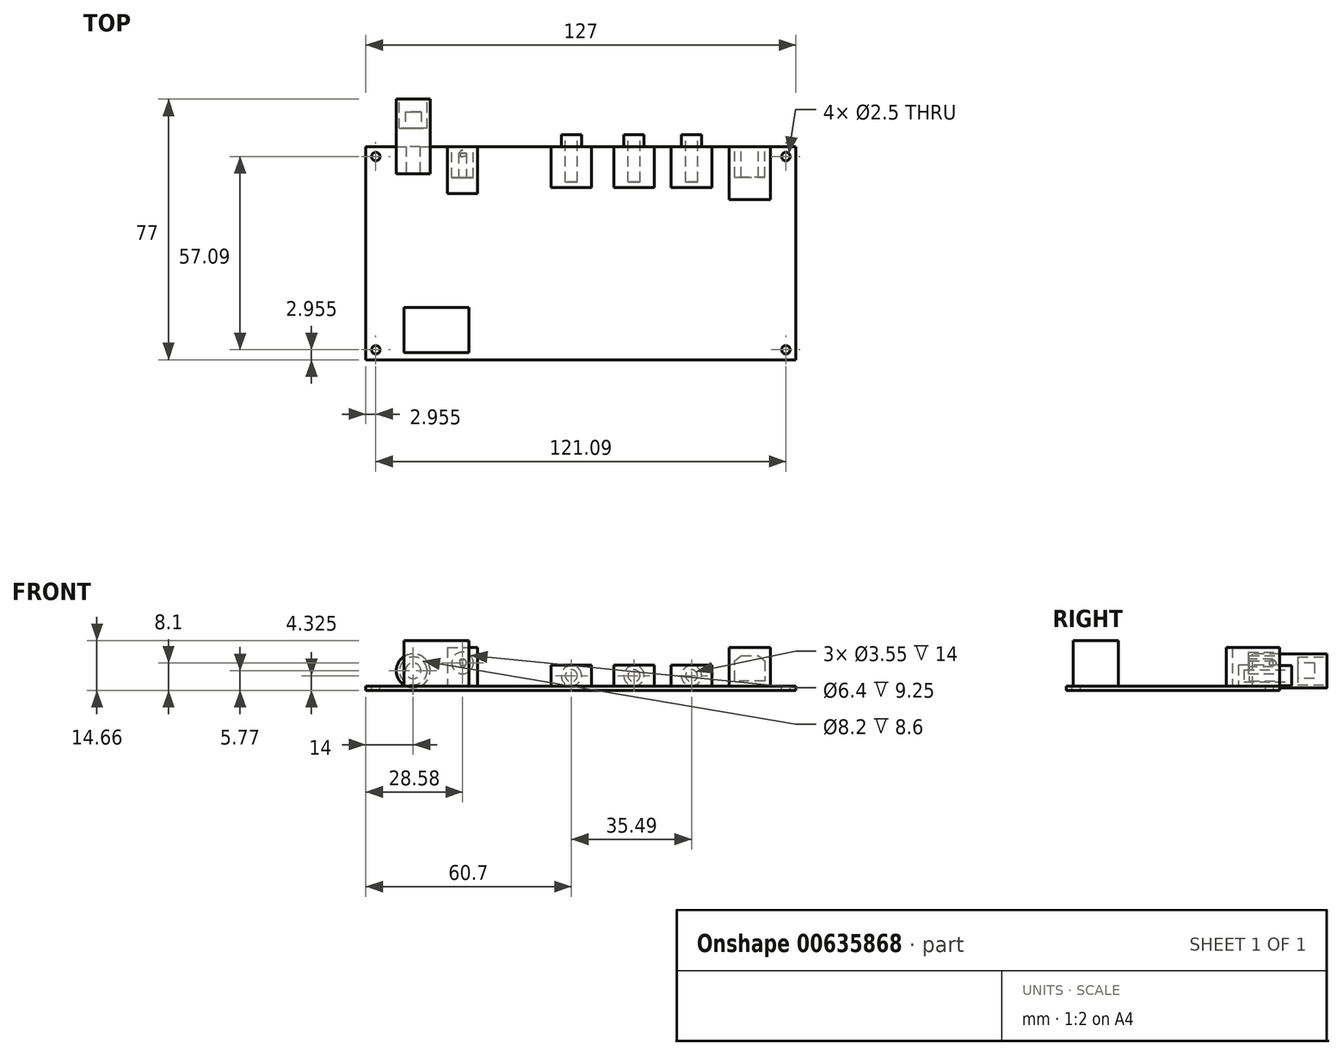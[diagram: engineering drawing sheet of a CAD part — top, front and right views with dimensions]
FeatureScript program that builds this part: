
annotation { "Feature Type Name" : "Feature", "Feature Type Description" : "" }
export const myFeature = defineFeature(function(context is Context, id is Id, definition is map)
    precondition{}
    {
        {
            var Q0;
            Q0=qCreatedBy(makeId("Top.planeOp"),FACE);
            var sketch = newSketch(context, id + "F0", { "sketchPlane" : qUnion([Q0])});
            skLineSegment(sketch, "E0.bottom", {"start": v(0, 0) * mm, "end": v(127, 0) * mm});
            skLineSegment(sketch, "E0.top", {"start": v(0, -63) * mm, "end": v(127, -63) * mm});
            skLineSegment(sketch, "E0.left", {"start": v(0, 0) * mm, "end": v(0, -63) * mm});
            skLineSegment(sketch, "E0.right", {"start": v(127, 0) * mm, "end": v(127, -63) * mm});
            skSolve(sketch);
        }
        {
            var Q0;
            Q0 = qSketchRegion(id + "F0", true);
            extrude(context, id + "F1", {"entities" : qUnion([Q0]), "depth" : 1.2 * mm, "offsetDistance" : 25 * mm});
        }
        {
            var Q0;
            Q0=makeQuery(id+"F1.opExtrude","CAP_FACE",FACE,{"disambiguationData":[OSD([sQuery(id+"F0.wireOp",EDGE,"E0.bottom"),sQuery(id+"F0.wireOp",EDGE,"E0.top"),sQuery(id+"F0.wireOp",EDGE,"E0.left"),sQuery(id+"F0.wireOp",EDGE,"E0.right")])],"isStart":false});
            var sketch = newSketch(context, id + "F2", { "sketchPlane" : qUnion([Q0]), "disableImprinting" : false});
            skLineSegment(sketch, "E1.bottom", {"start": v(2.95, -2.95) * mm, "end": v(124.05, -2.95) * mm, "construction": true});
            skLineSegment(sketch, "E1.top", {"start": v(2.95, -60.05) * mm, "end": v(124.05, -60.05) * mm, "construction": true});
            skLineSegment(sketch, "E1.left", {"start": v(2.95, -2.95) * mm, "end": v(2.95, -60.05) * mm, "construction": true});
            skLineSegment(sketch, "E1.right", {"start": v(124.05, -2.95) * mm, "end": v(124.05, -60.05) * mm, "construction": true});
            skCircle(sketch, "E2", {"center": v(2.95, -2.96) * mm, "radius": 2.96 * mm, "construction": true});
            skCircle(sketch, "E3", {"center": v(2.95, -60.05) * mm, "radius": 2.96 * mm, "construction": true});
            skCircle(sketch, "E4", {"center": v(124.05, -60.05) * mm, "radius": 2.96 * mm, "construction": true});
            skCircle(sketch, "E5", {"center": v(124.05, -2.96) * mm, "radius": 2.96 * mm, "construction": true});
            skPoint(sketch, "E6", {"position": v(63.5, 0) * mm});
            skPoint(sketch, "E7", {"position": v(0, -31.5) * mm});
            skPoint(sketch, "E8", {"position": v(63.5, -2.95) * mm});
            skPoint(sketch, "E9", {"position": v(2.95, -31.5) * mm});
            skCircle(sketch, "E10", {"center": v(2.95, -2.95) * mm, "radius": 1.25 * mm});
            skCircle(sketch, "E11", {"center": v(2.95, -60.05) * mm, "radius": 1.25 * mm});
            skCircle(sketch, "E12", {"center": v(124.05, -60.05) * mm, "radius": 1.25 * mm});
            skCircle(sketch, "E13", {"center": v(124.05, -2.95) * mm, "radius": 1.25 * mm});
            skSolve(sketch);
        }
        {
            var Q0;
            Q0 = qSketchRegion(id + "F2", true);
            extrude(context, id + "F3", {"entities" : qUnion([Q0]), "operationType" : NewBodyOperationType.REMOVE, "endBound" : BoundingType.UP_TO_NEXT, "oppositeDirection" : true, "depth" : 25 * mm, "offsetDistance" : 25 * mm});
        }
        {
            var Q0;
            Q0=makeQuery(id+"F1.opExtrude","CAP_FACE",FACE,{"disambiguationData":[OSD([sQuery(id+"F0.wireOp",EDGE,"E0.bottom"),sQuery(id+"F0.wireOp",EDGE,"E0.top"),sQuery(id+"F0.wireOp",EDGE,"E0.left"),sQuery(id+"F0.wireOp",EDGE,"E0.right")])],"isStart":false});
            var sketch = newSketch(context, id + "F4", { "sketchPlane" : qUnion([Q0])});
            skLineSegment(sketch, "E14.bottom", {"start": v(102.19, 0) * mm, "end": v(90.19, 0) * mm});
            skLineSegment(sketch, "E14.top", {"start": v(102.19, -12.13) * mm, "end": v(90.19, -12.13) * mm});
            skLineSegment(sketch, "E14.left", {"start": v(102.19, 0) * mm, "end": v(102.19, -12.13) * mm});
            skLineSegment(sketch, "E14.right", {"start": v(90.19, 0) * mm, "end": v(90.19, -12.13) * mm});
            skLineSegment(sketch, "E15.bottom", {"start": v(85.2, 0) * mm, "end": v(73.2, 0) * mm});
            skLineSegment(sketch, "E15.top", {"start": v(85.2, -12.13) * mm, "end": v(73.2, -12.13) * mm});
            skLineSegment(sketch, "E15.left", {"start": v(85.2, 0) * mm, "end": v(85.2, -12.13) * mm});
            skLineSegment(sketch, "E15.right", {"start": v(73.2, 0) * mm, "end": v(73.2, -12.13) * mm});
            skLineSegment(sketch, "E16.bottom", {"start": v(66.7, 0) * mm, "end": v(54.7, 0) * mm});
            skLineSegment(sketch, "E16.top", {"start": v(66.7, -12.13) * mm, "end": v(54.7, -12.13) * mm});
            skLineSegment(sketch, "E16.left", {"start": v(66.7, 0) * mm, "end": v(66.7, -12.13) * mm});
            skLineSegment(sketch, "E16.right", {"start": v(54.7, 0) * mm, "end": v(54.7, -12.13) * mm});
            skSolve(sketch);
        }
        {
            var Q0;
            Q0 = qSketchRegion(id + "F4", true);
            extrude(context, id + "F5", {"entities" : qUnion([Q0]), "operationType" : NewBodyOperationType.ADD, "depth" : 6.25 * mm, "offsetDistance" : 25 * mm});
        }
        {
            var Q0;
            Q0=makeQuery(id+"F5.boolean.opBoolean","MERGE",FACE,{"derivedFrom":[makeQuery(id+"F1.opExtrude","SWEPT_FACE",FACE,{"disambiguationData":[OSD([sQuery(id+"F0.wireOp",EDGE,"E0.bottom")])]}),makeQuery(id+"F5.opExtrude","SWEPT_FACE",FACE,{"disambiguationData":[OSD([sQuery(id+"F4.wireOp",EDGE,"E14.bottom")])]}),makeQuery(id+"F5.opExtrude","SWEPT_FACE",FACE,{"disambiguationData":[OSD([sQuery(id+"F4.wireOp",EDGE,"E15.bottom")])]}),makeQuery(id+"F5.opExtrude","SWEPT_FACE",FACE,{"disambiguationData":[OSD([sQuery(id+"F4.wireOp",EDGE,"E16.bottom")])]})]});
            var sketch = newSketch(context, id + "F6", { "sketchPlane" : qUnion([Q0])});
            skPoint(sketch, "E17", {"position": v(-102.19, 4.33) * mm});
            skPoint(sketch, "E18", {"position": v(-96.19, 7.45) * mm});
            skPoint(sketch, "E19", {"position": v(-79.2, 7.45) * mm});
            skPoint(sketch, "E20", {"position": v(-60.7, 7.45) * mm});
            skCircle(sketch, "E21", {"center": v(-96.19, 4.33) * mm, "radius": 3 * mm});
            skCircle(sketch, "E22", {"center": v(-79.2, 4.33) * mm, "radius": 3 * mm});
            skCircle(sketch, "E23", {"center": v(-60.7, 4.33) * mm, "radius": 3 * mm});
            skSolve(sketch);
        }
        {
            var Q0;
            Q0 = qSketchRegion(id + "F6", true);
            extrude(context, id + "F7", {"entities" : qUnion([Q0]), "operationType" : NewBodyOperationType.ADD, "depth" : 3.52 * mm, "offsetDistance" : 25 * mm});
        }
        {
            var Q0;
            Q0=makeQuery(id+"F7.opExtrude","CAP_FACE",FACE,{"disambiguationData":[OSD([sQuery(id+"F6.wireOp",EDGE,"E21")])],"isStart":false});
            var sketch = newSketch(context, id + "F8", { "sketchPlane" : qUnion([Q0])});
            skCircle(sketch, "E24", {"center": v(-96.19, 4.33) * mm, "radius": 1.77 * mm});
            skCircle(sketch, "E25", {"center": v(-79.2, 4.33) * mm, "radius": 1.77 * mm});
            skCircle(sketch, "E26", {"center": v(-60.7, 4.33) * mm, "radius": 1.77 * mm});
            skSolve(sketch);
        }
        {
            var Q0;
            Q0 = qSketchRegion(id + "F8", true);
            extrude(context, id + "F9", {"entities" : qUnion([Q0]), "operationType" : NewBodyOperationType.REMOVE, "oppositeDirection" : true, "depth" : 14 * mm, "offsetDistance" : 25 * mm});
        }
        {
            var Q0;
            Q0=makeQuery(id+"F1.opExtrude","CAP_FACE",FACE,{"disambiguationData":[OSD([sQuery(id+"F0.wireOp",EDGE,"E0.bottom"),sQuery(id+"F0.wireOp",EDGE,"E0.top"),sQuery(id+"F0.wireOp",EDGE,"E0.left"),sQuery(id+"F0.wireOp",EDGE,"E0.right")])],"isStart":false});
            var sketch = newSketch(context, id + "F10", { "sketchPlane" : qUnion([Q0])});
            skLineSegment(sketch, "E27.bottom", {"start": v(107.33, 0) * mm, "end": v(119.45, 0) * mm});
            skLineSegment(sketch, "E27.top", {"start": v(107.33, -15.7) * mm, "end": v(119.45, -15.7) * mm});
            skLineSegment(sketch, "E27.left", {"start": v(107.33, 0) * mm, "end": v(107.33, -15.7) * mm});
            skLineSegment(sketch, "E27.right", {"start": v(119.45, 0) * mm, "end": v(119.45, -15.7) * mm});
            skSolve(sketch);
        }
        {
            var Q0;
            Q0 = qSketchRegion(id + "F10", true);
            extrude(context, id + "F11", {"entities" : qUnion([Q0]), "operationType" : NewBodyOperationType.ADD, "depth" : 11.43 * mm, "offsetDistance" : 25 * mm});
        }
        {
            var Q0;
            Q0=makeQuery(id+"F11.boolean.opBoolean","MERGE",FACE,{"derivedFrom":[makeQuery(id+"F5.boolean.opBoolean","MERGE",FACE,{"derivedFrom":[makeQuery(id+"F1.opExtrude","SWEPT_FACE",FACE,{"disambiguationData":[OSD([sQuery(id+"F0.wireOp",EDGE,"E0.bottom")])]}),makeQuery(id+"F5.opExtrude","SWEPT_FACE",FACE,{"disambiguationData":[OSD([sQuery(id+"F4.wireOp",EDGE,"E14.bottom")])]}),makeQuery(id+"F5.opExtrude","SWEPT_FACE",FACE,{"disambiguationData":[OSD([sQuery(id+"F4.wireOp",EDGE,"E15.bottom")])]}),makeQuery(id+"F5.opExtrude","SWEPT_FACE",FACE,{"disambiguationData":[OSD([sQuery(id+"F4.wireOp",EDGE,"E16.bottom")])]})]}),makeQuery(id+"F11.opExtrude","SWEPT_FACE",FACE,{"disambiguationData":[OSD([sQuery(id+"F10.wireOp",EDGE,"E27.bottom")])]})]});
            var sketch = newSketch(context, id + "F12", { "sketchPlane" : qUnion([Q0])});
            skLineSegment(sketch, "E28", {"start": v(-117.78, 2.8) * mm, "end": v(-109, 2.8) * mm});
            skLineSegment(sketch, "E29", {"start": v(-109, 2.8) * mm, "end": v(-109, 8.72) * mm});
            skLineSegment(sketch, "E30", {"start": v(-109, 8.72) * mm, "end": v(-110.89, 10.2) * mm});
            skLineSegment(sketch, "E31", {"start": v(-110.89, 10.2) * mm, "end": v(-115.89, 10.2) * mm});
            skLineSegment(sketch, "E32", {"start": v(-115.89, 10.2) * mm, "end": v(-117.78, 8.72) * mm});
            skLineSegment(sketch, "E33", {"start": v(-117.78, 8.72) * mm, "end": v(-117.78, 2.8) * mm});
            skPoint(sketch, "E34", {"position": v(-113.39, 12.63) * mm});
            skPoint(sketch, "E35", {"position": v(-113.39, 10.2) * mm});
            skSolve(sketch);
        }
        {
            var Q0;
            Q0 = qSketchRegion(id + "F12", true);
            extrude(context, id + "F13", {"entities" : qUnion([Q0]), "operationType" : NewBodyOperationType.REMOVE, "oppositeDirection" : true, "depth" : 9 * mm, "offsetDistance" : 25 * mm});
        }
        {
            var Q0;
            Q0=makeQuery(id+"F1.opExtrude","CAP_FACE",FACE,{"disambiguationData":[OSD([sQuery(id+"F0.wireOp",EDGE,"E0.bottom"),sQuery(id+"F0.wireOp",EDGE,"E0.top"),sQuery(id+"F0.wireOp",EDGE,"E0.left"),sQuery(id+"F0.wireOp",EDGE,"E0.right")])],"isStart":false});
            var sketch = newSketch(context, id + "F14", { "sketchPlane" : qUnion([Q0])});
            skLineSegment(sketch, "E36.bottom", {"start": v(24.16, 0) * mm, "end": v(33, 0) * mm});
            skLineSegment(sketch, "E36.top", {"start": v(24.16, -13.9) * mm, "end": v(33, -13.9) * mm});
            skLineSegment(sketch, "E36.left", {"start": v(24.16, 0) * mm, "end": v(24.16, -13.9) * mm});
            skLineSegment(sketch, "E36.right", {"start": v(33, 0) * mm, "end": v(33, -13.9) * mm});
            skSolve(sketch);
        }
        {
            var Q0;
            Q0 = qSketchRegion(id + "F14", true);
            extrude(context, id + "F15", {"entities" : qUnion([Q0]), "operationType" : NewBodyOperationType.ADD, "depth" : 11.4 * mm, "offsetDistance" : 25 * mm});
        }
        {
            var Q0;
            Q0=makeQuery(id+"F15.boolean.opBoolean","MERGE",FACE,{"derivedFrom":[makeQuery(id+"F11.boolean.opBoolean","MERGE",FACE,{"derivedFrom":[makeQuery(id+"F5.boolean.opBoolean","MERGE",FACE,{"derivedFrom":[makeQuery(id+"F1.opExtrude","SWEPT_FACE",FACE,{"disambiguationData":[OSD([sQuery(id+"F0.wireOp",EDGE,"E0.bottom")])]}),makeQuery(id+"F5.opExtrude","SWEPT_FACE",FACE,{"disambiguationData":[OSD([sQuery(id+"F4.wireOp",EDGE,"E14.bottom")])]}),makeQuery(id+"F5.opExtrude","SWEPT_FACE",FACE,{"disambiguationData":[OSD([sQuery(id+"F4.wireOp",EDGE,"E15.bottom")])]}),makeQuery(id+"F5.opExtrude","SWEPT_FACE",FACE,{"disambiguationData":[OSD([sQuery(id+"F4.wireOp",EDGE,"E16.bottom")])]})]}),makeQuery(id+"F11.opExtrude","SWEPT_FACE",FACE,{"disambiguationData":[OSD([sQuery(id+"F10.wireOp",EDGE,"E27.bottom")])]})]}),makeQuery(id+"F15.opExtrude","SWEPT_FACE",FACE,{"disambiguationData":[OSD([sQuery(id+"F14.wireOp",EDGE,"E36.bottom")])]})]});
            var sketch = newSketch(context, id + "F16", { "sketchPlane" : qUnion([Q0])});
            skCircle(sketch, "E37", {"center": v(-28.58, 8.1) * mm, "radius": 3.2 * mm});
            skPoint(sketch, "E38", {"position": v(-28.58, 12.6) * mm});
            skPoint(sketch, "E39", {"position": v(-28.58, 11.3) * mm});
            skSolve(sketch);
        }
        {
            var Q0;
            Q0 = qSketchRegion(id + "F16", true);
            extrude(context, id + "F17", {"entities" : qUnion([Q0]), "operationType" : NewBodyOperationType.REMOVE, "oppositeDirection" : true, "depth" : 9.25 * mm, "offsetDistance" : 25 * mm});
        }
        {
            var Q0;
            Q0=makeQuery(id+"F17.boolean.opBoolean","COPY",FACE,{"derivedFrom":makeQuery(id+"F17.opExtrude","CAP_FACE",FACE,{"disambiguationData":[OSD([sQuery(id+"F16.wireOp",EDGE,"E37")])],"isStart":false})});
            var sketch = newSketch(context, id + "F18", { "sketchPlane" : qUnion([Q0])});
            skCircle(sketch, "E40", {"center": v(-28.58, 8.1) * mm, "radius": 1.15 * mm});
            skSolve(sketch);
        }
        {
            var Q0;
            Q0 = qSketchRegion(id + "F18", true);
            var Q1;
            Q1=makeQuery(id+"F15.boolean.opBoolean","MERGE",FACE,{"derivedFrom":[makeQuery(id+"F11.boolean.opBoolean","MERGE",FACE,{"derivedFrom":[makeQuery(id+"F5.boolean.opBoolean","MERGE",FACE,{"derivedFrom":[makeQuery(id+"F1.opExtrude","SWEPT_FACE",FACE,{"disambiguationData":[OSD([sQuery(id+"F0.wireOp",EDGE,"E0.bottom")])]}),makeQuery(id+"F5.opExtrude","SWEPT_FACE",FACE,{"disambiguationData":[OSD([sQuery(id+"F4.wireOp",EDGE,"E14.bottom")])]}),makeQuery(id+"F5.opExtrude","SWEPT_FACE",FACE,{"disambiguationData":[OSD([sQuery(id+"F4.wireOp",EDGE,"E15.bottom")])]}),makeQuery(id+"F5.opExtrude","SWEPT_FACE",FACE,{"disambiguationData":[OSD([sQuery(id+"F4.wireOp",EDGE,"E16.bottom")])]})]}),makeQuery(id+"F11.opExtrude","SWEPT_FACE",FACE,{"disambiguationData":[OSD([sQuery(id+"F10.wireOp",EDGE,"E27.bottom")])]})]}),makeQuery(id+"F15.opExtrude","SWEPT_FACE",FACE,{"disambiguationData":[OSD([sQuery(id+"F14.wireOp",EDGE,"E36.bottom")])]})]});
            extrude(context, id + "F19", {"entities" : qUnion([Q0]), "operationType" : NewBodyOperationType.ADD, "endBound" : BoundingType.UP_TO_SURFACE, "depth" : 25 * mm, "endBoundEntityFace" : qUnion([Q1]), "hasOffset" : true, "offsetDistance" : 1 * mm});
        }
        {
            var Q0;
            Q0=makeQuery(id+"F19.opExtrude","CAP_EDGE",EDGE,{"disambiguationData":[OSD([sQuery(id+"F18.wireOp",EDGE,"E40")])],"isStart":false});
            fillet(context, id + "F20", {"entities" : qUnion([Q0]), "radius" : 1 * mm, "tangentPropagation" : true, "allowEdgeOverflow" : false});
        }
        {
            var Q0;
            Q0=makeQuery(id+"F15.boolean.opBoolean","MERGE",FACE,{"derivedFrom":[makeQuery(id+"F11.boolean.opBoolean","MERGE",FACE,{"derivedFrom":[makeQuery(id+"F5.boolean.opBoolean","MERGE",FACE,{"derivedFrom":[makeQuery(id+"F1.opExtrude","SWEPT_FACE",FACE,{"disambiguationData":[OSD([sQuery(id+"F0.wireOp",EDGE,"E0.bottom")])]}),makeQuery(id+"F5.opExtrude","SWEPT_FACE",FACE,{"disambiguationData":[OSD([sQuery(id+"F4.wireOp",EDGE,"E14.bottom")])]}),makeQuery(id+"F5.opExtrude","SWEPT_FACE",FACE,{"disambiguationData":[OSD([sQuery(id+"F4.wireOp",EDGE,"E15.bottom")])]}),makeQuery(id+"F5.opExtrude","SWEPT_FACE",FACE,{"disambiguationData":[OSD([sQuery(id+"F4.wireOp",EDGE,"E16.bottom")])]})]}),makeQuery(id+"F11.opExtrude","SWEPT_FACE",FACE,{"disambiguationData":[OSD([sQuery(id+"F10.wireOp",EDGE,"E27.bottom")])]})]}),makeQuery(id+"F15.opExtrude","SWEPT_FACE",FACE,{"disambiguationData":[OSD([sQuery(id+"F14.wireOp",EDGE,"E36.bottom")])]})]});
            var sketch = newSketch(context, id + "F21", { "sketchPlane" : qUnion([Q0])});
            skCircle(sketch, "E41", {"center": v(-14, 5.77) * mm, "radius": 5 * mm});
            skPoint(sketch, "E42", {"position": v(-14, 0.77) * mm});
            skPoint(sketch, "E43", {"position": v(-9, 5.77) * mm});
            skSolve(sketch);
        }
        {
            var Q0;
            Q0 = qSketchRegion(id + "F21", true);
            extrude(context, id + "F22", {"entities" : qUnion([Q0]), "operationType" : NewBodyOperationType.ADD, "depth" : 14 * mm, "offsetDistance" : 25 * mm, "hasSecondDirection" : true, "secondDirectionOppositeDirection" : true, "secondDirectionDepth" : (22 - 14) * mm});
        }
        {
            var Q0;
            Q0=makeQuery(id+"F22.opExtrude","CAP_FACE",FACE,{"disambiguationData":[OSD([sQuery(id+"F21.wireOp",EDGE,"E41")])],"isStart":false});
            var sketch = newSketch(context, id + "F23", { "sketchPlane" : qUnion([Q0])});
            skCircle(sketch, "E44", {"center": v(-14, 5.77) * mm, "radius": 4.1 * mm});
            skSolve(sketch);
        }
        {
            var Q0;
            Q0 = qSketchRegion(id + "F23", true);
            extrude(context, id + "F24", {"entities" : qUnion([Q0]), "operationType" : NewBodyOperationType.REMOVE, "oppositeDirection" : true, "depth" : 8.6 * mm, "offsetDistance" : 25 * mm});
        }
        {
            var Q0;
            Q0=makeQuery(id+"F24.boolean.opBoolean","COPY",FACE,{"derivedFrom":makeQuery(id+"F24.opExtrude","CAP_FACE",FACE,{"disambiguationData":[OSD([sQuery(id+"F23.wireOp",EDGE,"E44")])],"isStart":false})});
            var sketch = newSketch(context, id + "F25", { "sketchPlane" : qUnion([Q0])});
            skCircle(sketch, "E45", {"center": v(-14, 5.77) * mm, "radius": 2.3 * mm});
            skSolve(sketch);
        }
        {
            var Q0;
            Q0 = qSketchRegion(id + "F25", true);
            var Q1;
            Q1=makeQuery(id+"F22.opExtrude","CAP_FACE",FACE,{"disambiguationData":[OSD([sQuery(id+"F21.wireOp",EDGE,"E41")])],"isStart":false});
            extrude(context, id + "F26", {"entities" : qUnion([Q0]), "operationType" : NewBodyOperationType.ADD, "endBound" : BoundingType.UP_TO_SURFACE, "depth" : 25 * mm, "endBoundEntityFace" : qUnion([Q1]), "hasOffset" : true, "offsetDistance" : 3.7 * mm});
        }
        {
            var Q0;
            Q0=makeQuery(id+"F1.opExtrude","CAP_FACE",FACE,{"disambiguationData":[OSD([sQuery(id+"F0.wireOp",EDGE,"E0.bottom"),sQuery(id+"F0.wireOp",EDGE,"E0.top"),sQuery(id+"F0.wireOp",EDGE,"E0.left"),sQuery(id+"F0.wireOp",EDGE,"E0.right")])],"isStart":false});
            var sketch = newSketch(context, id + "F27", { "sketchPlane" : qUnion([Q0])});
            skLineSegment(sketch, "E46.bottom", {"start": v(11.3, -60.9) * mm, "end": v(30.46, -60.9) * mm});
            skLineSegment(sketch, "E46.top", {"start": v(11.3, -47.6) * mm, "end": v(30.46, -47.6) * mm});
            skLineSegment(sketch, "E46.left", {"start": v(11.3, -60.9) * mm, "end": v(11.3, -47.6) * mm});
            skLineSegment(sketch, "E46.right", {"start": v(30.46, -60.9) * mm, "end": v(30.46, -47.6) * mm});
            skSolve(sketch);
        }
        {
            var Q0;
            Q0 = qSketchRegion(id + "F27", true);
            extrude(context, id + "F28", {"entities" : qUnion([Q0]), "operationType" : NewBodyOperationType.ADD, "depth" : 13.46 * mm, "offsetDistance" : 25 * mm});
        }
    });
